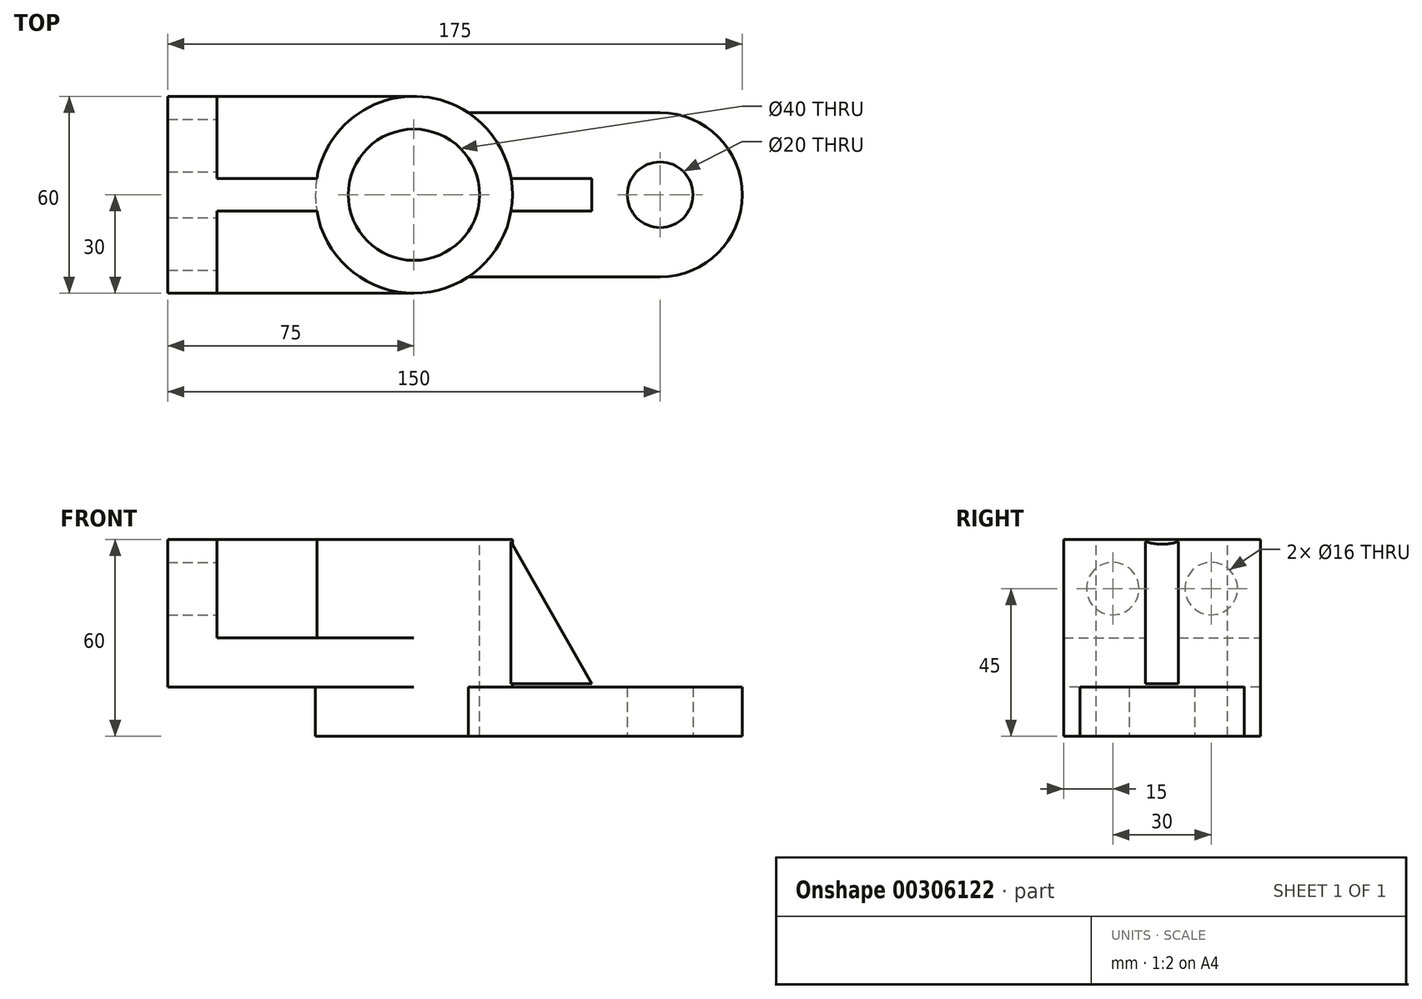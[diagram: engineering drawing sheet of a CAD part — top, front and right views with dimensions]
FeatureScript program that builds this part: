
annotation { "Feature Type Name" : "Feature", "Feature Type Description" : "" }
export const myFeature = defineFeature(function(context is Context, id is Id, definition is map)
    precondition{}
    {
        {
            var Q0;
            Q0=qCreatedBy(makeId("Top.planeOp"),FACE);
            var sketch = newSketch(context, id + "F0", { "sketchPlane" : qUnion([Q0])});
            skCircle(sketch, "E0", {"center": v(0, 0) * mm, "radius": 20 * mm});
            skCircle(sketch, "E1", {"center": v(0, 0) * mm, "radius": 30 * mm});
            skLineSegment(sketch, "E2", {"start": v(-60, -5) * mm, "end": v(-29.58, -5) * mm});
            skLineSegment(sketch, "E3", {"start": v(0, 0) * mm, "end": v(-75, 0) * mm, "construction": true});
            skLineSegment(sketch, "E4", {"start": v(-29.58, 5) * mm, "end": v(-60, 5) * mm});
            skLineSegment(sketch, "E5", {"start": v(-75, 0) * mm, "end": v(-75, 30) * mm});
            skLineSegment(sketch, "E6", {"start": v(-75, 0) * mm, "end": v(-75, -30) * mm});
            skLineSegment(sketch, "E7", {"start": v(-75, 30) * mm, "end": v(-74.09, 30) * mm});
            skLineSegment(sketch, "E8", {"start": v(-75, 30) * mm, "end": v(-60, 30) * mm});
            skLineSegment(sketch, "E9", {"start": v(-60, 30) * mm, "end": v(-60, 5) * mm});
            skLineSegment(sketch, "E10", {"start": v(-75, -30) * mm, "end": v(-60, -30) * mm});
            skLineSegment(sketch, "E11", {"start": v(-60, -30) * mm, "end": v(-60, -5) * mm});
            skPoint(sketch, "E12.orphan", {"position": v(-60, 5) * mm});
            skPoint(sketch, "E13.orphan", {"position": v(-60, -5) * mm});
            skSolve(sketch);
        }
        {
            var Q0;
            Q0=makeQuery(id+"F0.imprint","IMPRINT",FACE,{"disambiguationData":[TD([[makeQuery(id+"F0.imprint","IMPRINT",EDGE,{"derivedFrom":sQuery(id+"F0.wireOp",EDGE,"E0")}),-1.0]])]});
            extrude(context, id + "F1", {"entities" : qUnion([Q0]), "oppositeDirection" : true, "depth" : 60 * mm});
        }
        {
            var Q0;
            Q0=makeQuery(id+"F1.opExtrude","CAP_FACE",FACE,{"disambiguationData":[OSD([sQuery(id+"F0.wireOp",EDGE,"E0"),sQuery(id+"F0.wireOp",EDGE,"E1")])],"isStart":false});
            var sketch = newSketch(context, id + "F2", { "sketchPlane" : qUnion([Q0])});
            skCircle(sketch, "E14", {"center": v(75, 0) * mm, "radius": 10 * mm});
            skArc(sketch, "E15", {"start": v(75, -25) * mm, "mid": v(100, 0) * mm, "end": v(75, 25) * mm});
            skLineSegment(sketch, "E16", {"start": v(75, 25) * mm, "end": v(16.58, 25) * mm});
            skLineSegment(sketch, "E17", {"start": v(75, -25) * mm, "end": v(16.58, -25) * mm});
            skArc(sketch, "E18", {"start": v(16.58, -25) * mm, "mid": v(29.82, 0) * mm, "end": v(16.58, 25) * mm});
            skSolve(sketch);
        }
        {
            var Q0;
            Q0=makeQuery(id+"F2.imprint","IMPRINT",FACE,{"disambiguationData":[TD([[makeQuery(id+"F2.imprint","IMPRINT",EDGE,{"derivedFrom":sQuery(id+"F2.wireOp",EDGE,"E14")}),-1.0]])]});
            extrude(context, id + "F3", {"entities" : qUnion([Q0]), "operationType" : NewBodyOperationType.ADD, "oppositeDirection" : true, "depth" : 15 * mm});
        }
        {
            var Q0;
            {var subQ2=sQuery(id+"F0.wireOp",EDGE,"E2");Q0=makeQuery(id+"F0.imprint","IMPRINT",FACE,{"disambiguationData":[TD([[makeQuery(id+"F0.imprint","IMPRINT",EDGE,{"derivedFrom":subQ2}),1.0]])]});}
            extrude(context, id + "F4", {"entities" : qUnion([Q0]), "operationType" : NewBodyOperationType.ADD, "oppositeDirection" : true, "depth" : 45 * mm});
        }
        {
            var Q0;
            Q0=makeQuery(id+"F4.opExtrude","CAP_FACE",FACE,{"disambiguationData":[OSD([sQuery(id+"F0.wireOp",EDGE,"E1"),sQuery(id+"F0.wireOp",EDGE,"E2"),sQuery(id+"F0.wireOp",EDGE,"E4"),sQuery(id+"F0.wireOp",EDGE,"E5"),sQuery(id+"F0.wireOp",EDGE,"E6"),sQuery(id+"F0.wireOp",EDGE,"E8"),sQuery(id+"F0.wireOp",EDGE,"E9"),sQuery(id+"F0.wireOp",EDGE,"E10"),sQuery(id+"F0.wireOp",EDGE,"E11")])],"isStart":false});
            var sketch = newSketch(context, id + "F5", { "sketchPlane" : qUnion([Q0])});
            skLineSegment(sketch, "E19", {"start": v(-60, 30) * mm, "end": v(0, 30) * mm});
            skLineSegment(sketch, "E20", {"start": v(0, -30) * mm, "end": v(-60, -30) * mm});
            skLineSegment(sketch, "E21", {"start": v(-60, -30) * mm, "end": v(-60, 30) * mm});
            skArc(sketch, "E22", {"start": v(0, 30) * mm, "mid": v(-30, 0) * mm, "end": v(0, -30) * mm});
            skSolve(sketch);
        }
        {
            var Q0;
            Q0 = qSketchRegion(id + "F5", true);
            extrude(context, id + "F6", {"entities" : qUnion([Q0]), "operationType" : NewBodyOperationType.ADD, "oppositeDirection" : true, "depth" : 15 * mm});
        }
        {
            var Q0;
            Q0=qCreatedBy(makeId("Front.planeOp"),FACE);
            var sketch = newSketch(context, id + "F7", { "sketchPlane" : qUnion([Q0])});
            skLineSegment(sketch, "E23", {"start": v(29.17, -43.93) * mm, "end": v(54.17, -43.93) * mm});
            skLineSegment(sketch, "E24", {"start": v(29.17, -43.93) * mm, "end": v(29.17, 0) * mm});
            skLineSegment(sketch, "E25", {"start": v(29.17, 0) * mm, "end": v(54.17, -43.93) * mm});
            skSolve(sketch);
        }
        {
            var Q0;
            Q0 = qSketchRegion(id + "F7", true);
            extrude(context, id + "F8", {"entities" : qUnion([Q0]), "operationType" : NewBodyOperationType.ADD, "endBound" : BoundingType.SYMMETRIC, "depth" : 10 * mm});
        }
        {
            var Q0;
            Q0=makeQuery(id+"F4.opExtrude","SWEPT_FACE",FACE,{"disambiguationData":[OSD([sQuery(id+"F0.wireOp",EDGE,"E11")])]});
            var sketch = newSketch(context, id + "F9", { "sketchPlane" : qUnion([Q0])});
            skCircle(sketch, "E26", {"center": v(-15, -15) * mm, "radius": 8 * mm});
            skCircle(sketch, "E27", {"center": v(15, -15) * mm, "radius": 8 * mm});
            skSolve(sketch);
        }
        {
            var Q0;
            Q0 = qSketchRegion(id + "F9", true);
            extrude(context, id + "F10", {"entities" : qUnion([Q0]), "operationType" : NewBodyOperationType.REMOVE, "endBound" : BoundingType.THROUGH_ALL, "oppositeDirection" : true, "depth" : 25 * mm});
        }
    });
